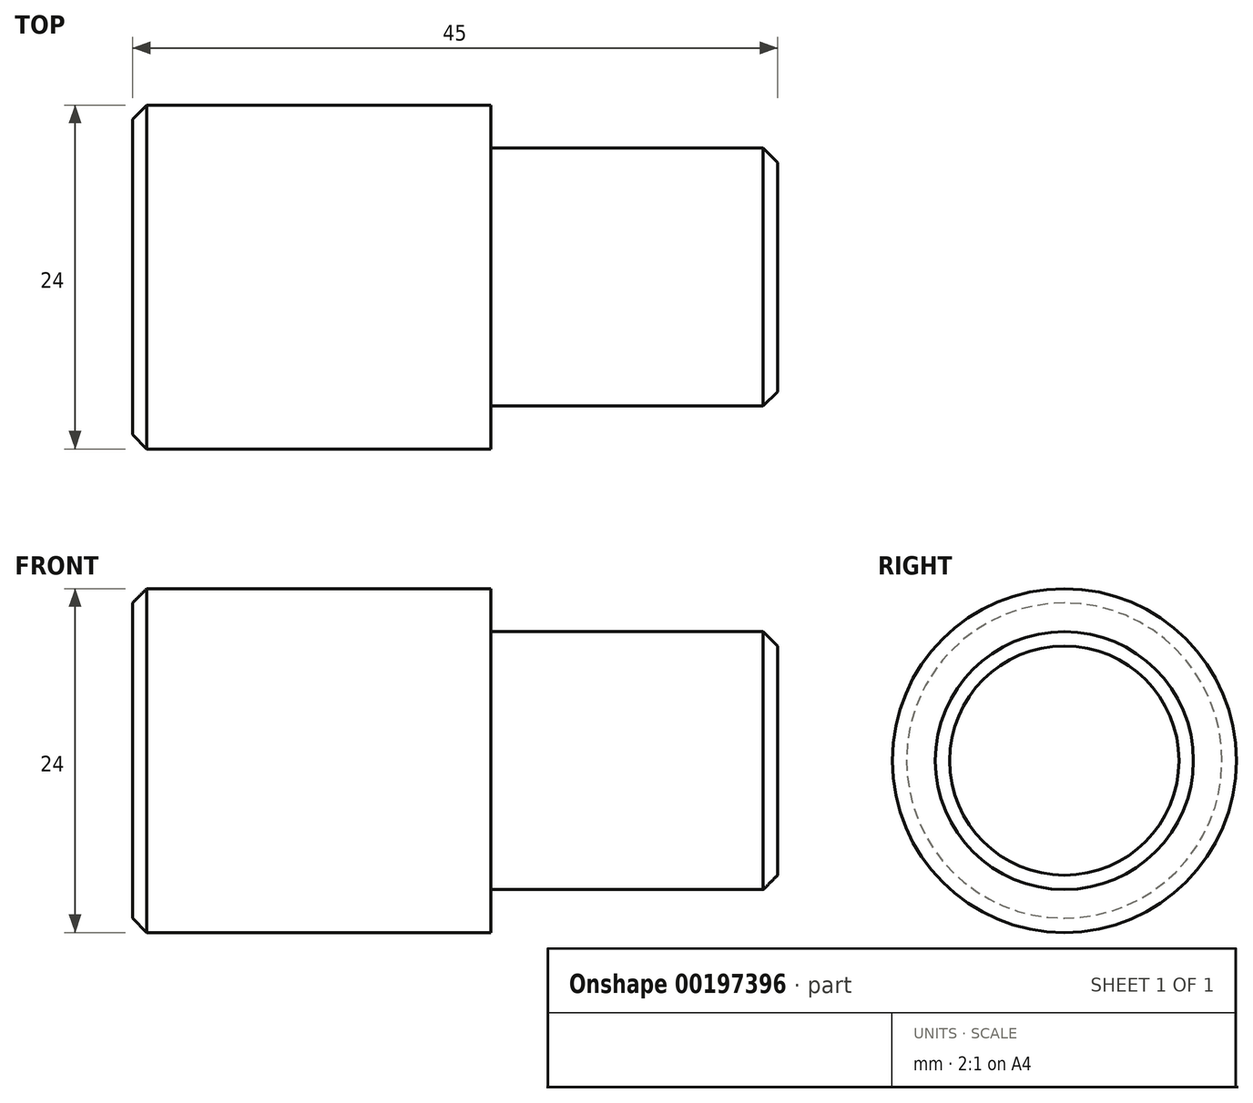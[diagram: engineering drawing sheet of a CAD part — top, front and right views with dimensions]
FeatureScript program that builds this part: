
annotation { "Feature Type Name" : "Feature", "Feature Type Description" : "" }
export const myFeature = defineFeature(function(context is Context, id is Id, definition is map)
    precondition{}
    {
        {
            var Q0;
            Q0=qCreatedBy(makeId("Front.planeOp"),FACE);
            var sketch = newSketch(context, id + "F0", { "sketchPlane" : qUnion([Q0])});
            skLineSegment(sketch, "E0", {"start": v(-9, 0) * mm, "end": v(37.25, 0) * mm, "construction": true});
            skLineSegment(sketch, "E1", {"start": v(0, 0) * mm, "end": v(0, 12) * mm});
            skLineSegment(sketch, "E2", {"start": v(0, 12) * mm, "end": v(25, 12) * mm});
            skLineSegment(sketch, "E3", {"start": v(25, 12) * mm, "end": v(25, 9) * mm});
            skLineSegment(sketch, "E4", {"start": v(25, 9) * mm, "end": v(45, 9) * mm});
            skLineSegment(sketch, "E5", {"start": v(45, 9) * mm, "end": v(45, 0) * mm});
            skLineSegment(sketch, "E6", {"start": v(45, 0) * mm, "end": v(0, 0) * mm});
            skSolve(sketch);
        }
        {
            var Q0;
            Q0 = qSketchRegion(id + "F0", true);
            var Q1;
            Q1=sQuery(id+"F0.wireOp",EDGE,"E0");
            revolve(context, id + "F1", {"entities" : qUnion([Q0]), "axis" : qUnion([Q1]), "revolveType" : RevolveType.FULL});
        }
        {
            var Q0;
            Q0=makeQuery(id+"F1.opRevolve","SWEPT_EDGE",EDGE,{"disambiguationData":[OSD([sQuery(id+"F0.wireOp",EDGE,"E1"),sQuery(id+"F0.wireOp",EDGE,"E2")])]});
            var Q1;
            Q1=makeQuery(id+"F1.opRevolve","SWEPT_EDGE",EDGE,{"disambiguationData":[OSD([sQuery(id+"F0.wireOp",EDGE,"E4"),sQuery(id+"F0.wireOp",EDGE,"E5")])]});
            chamfer(context, id + "F2", {"entities" : qUnion([Q0, Q1]), "width" : 1 * mm, "tangentPropagation" : true});
        }
    });
